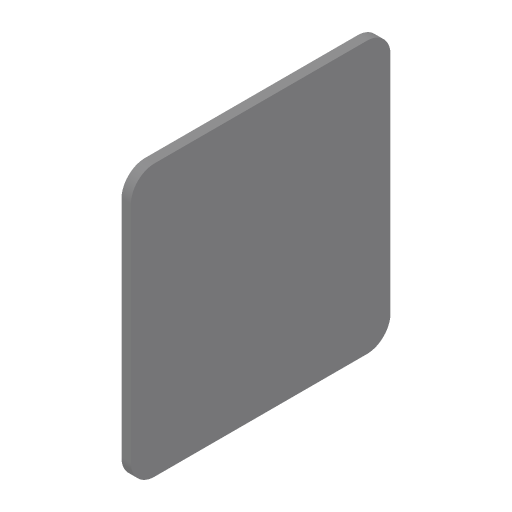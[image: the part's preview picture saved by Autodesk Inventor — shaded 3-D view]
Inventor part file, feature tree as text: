
AUTODESK INVENTOR PART (.ipt)
format: ipt  version: 2024.1 (Build 281209000, 209)  size: 105,472 bytes
history: native  units: mm
features: extrude x1, sketch x1
ambient origin geometry x8: Origin, YZ Plane, XZ Plane, XY Plane, X Axis, Y Axis, Z Axis, Center Point
bodies: Solid1 (feature_tree)
feature tree (2):
  extrude  "Extrusion1"  Depth=230.0mm
  sketch  "Sketch1"  dims[d0=220.0mm d1=230.0mm d2=20.0mm d3=8.0mm d4=0.0mm]
